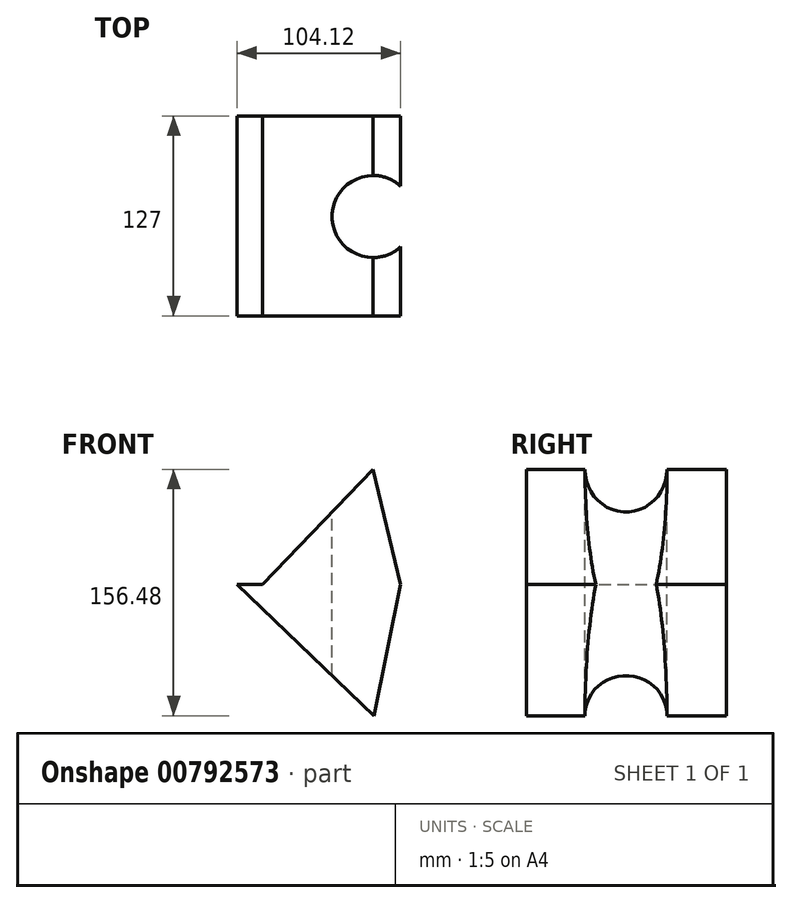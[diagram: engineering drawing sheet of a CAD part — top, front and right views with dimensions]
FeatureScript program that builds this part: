
annotation { "Feature Type Name" : "Feature", "Feature Type Description" : "" }
export const myFeature = defineFeature(function(context is Context, id is Id, definition is map)
    precondition{}
    {
        {
            var Q0;
            Q0=qCreatedBy(makeId("Front.planeOp"),FACE);
            var sketch = newSketch(context, id + "F0", { "sketchPlane" : qUnion([Q0])});
            skLineSegment(sketch, "E0", {"start": v(-87.9, 0) * mm, "end": v(-17.5, 73.04) * mm});
            skLineSegment(sketch, "E1", {"start": v(-17.5, 73.04) * mm, "end": v(0, 0) * mm});
            skLineSegment(sketch, "E2", {"start": v(0, 0) * mm, "end": v(-17.07, -83.44) * mm});
            skLineSegment(sketch, "E3", {"start": v(-17.07, -83.44) * mm, "end": v(-104.12, 0) * mm});
            skLineSegment(sketch, "E4", {"start": v(-104.12, 0) * mm, "end": v(-87.9, 0) * mm});
            skSolve(sketch);
        }
        {
            var Q0;
            Q0 = qSketchRegion(id + "F0", true);
            extrude(context, id + "F1", {"entities" : qUnion([Q0]), "depth" : 127 * mm, "offsetDistance" : 25.4 * mm});
        }
        {
            var Q0;
            Q0=qCreatedBy(makeId("Top.planeOp"),FACE);
            var sketch = newSketch(context, id + "F2", { "sketchPlane" : qUnion([Q0])});
            skCircle(sketch, "E5", {"center": v(-17.65, -63.93) * mm, "radius": 26.1 * mm});
            skSolve(sketch);
        }
        {
            var Q0;
            Q0=makeQuery(id+"F2.imprint","IMPRINT",FACE,{"disambiguationData":[TD([[makeQuery(id+"F2.imprint","IMPRINT",EDGE,{"derivedFrom":sQuery(id+"F2.wireOp",EDGE,"E5")}),1.0]])]});
            var Q1;
            Q1=sQuery(id+"F2.wireOp",EDGE,"E5");
            extrude(context, id + "F3", {"entities" : qUnion([Q0]), "operationType" : NewBodyOperationType.REMOVE, "surfaceOperationType" : NewSurfaceOperationType.ADD, "surfaceEntities" : qUnion([Q1]), "endBound" : BoundingType.SYMMETRIC, "oppositeDirection" : true, "depth" : 15240 * mm, "offsetDistance" : 25.4 * mm});
        }
    });
